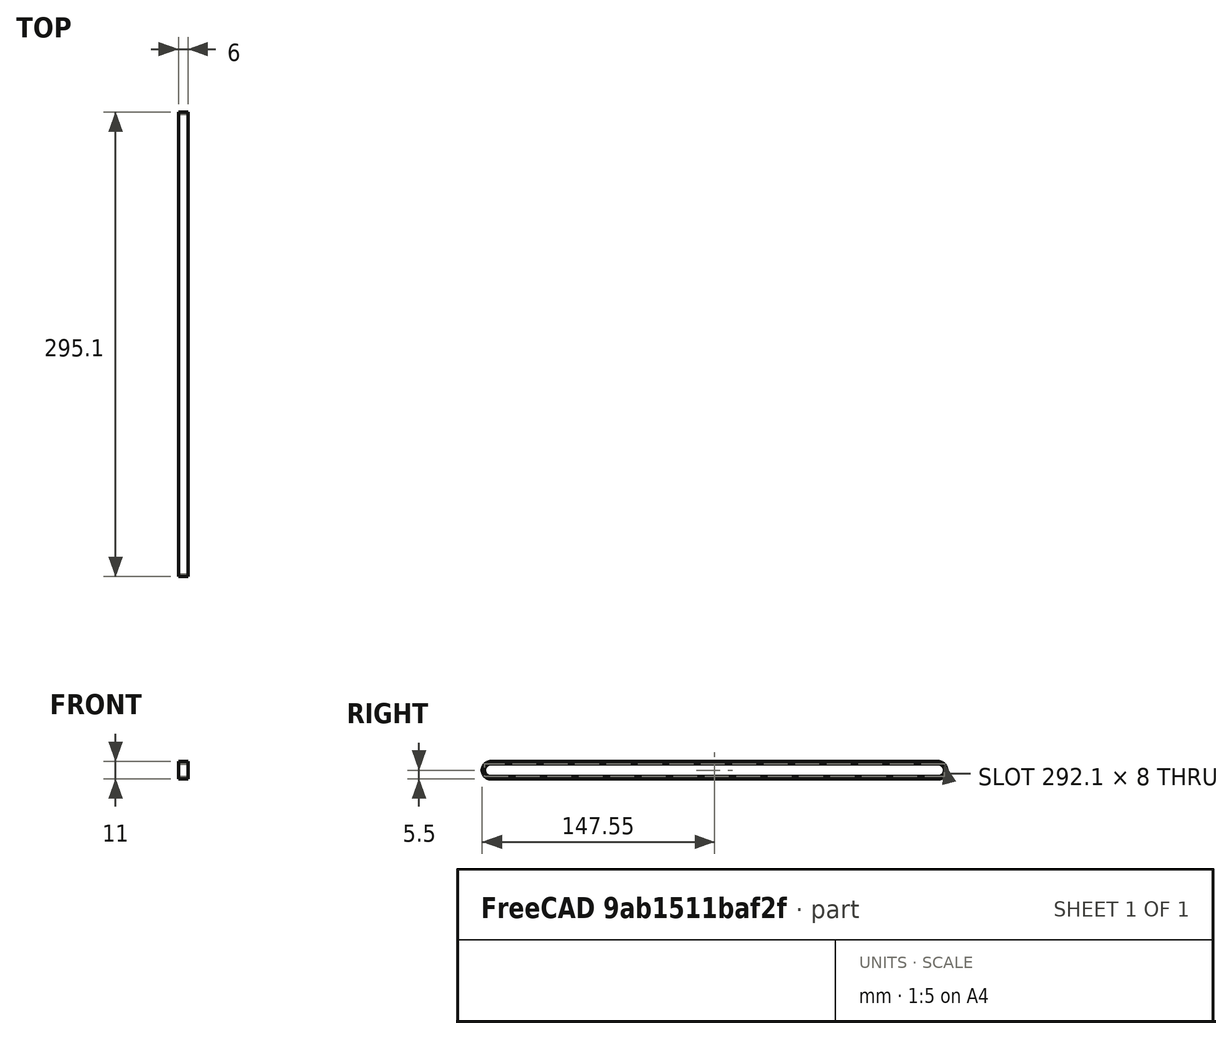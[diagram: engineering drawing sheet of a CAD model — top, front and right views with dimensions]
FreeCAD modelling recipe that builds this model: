
FCSTD DOCUMENT  (FreeCAD 0.18R16117 (Git))
Label: _GT2-Belt_Y-Axis
License: All rights reserved
LicenseURL: http://en.wikipedia.org/wiki/All_rights_reserved
objects: Sketcher::SketchObject×1, PartDesign::Pad×1, PartDesign::Body×1
note: 4 computed .brp shape members not serialized (recipe doc carries the construction recipe); baked Part::Feature solids carry a one-line shape summary decoded from their .brp

FEATURE [Sketcher::SketchObject] Sketch
  MapMode = 5
  Placement = pos=(0,0,0) rot=(0.57735,0.57735,0.57735;2.0944rad)
  Support = -> [YZ_Plane038]
  sketch-geometry (8):
    g0: LineSegment StartX=-140.25 StartY=5.5 StartZ=0 EndX=143.85 EndY=5.5 EndZ=0
    g1: LineSegment StartX=-140.25 StartY=4 StartZ=0 EndX=143.85 EndY=4 EndZ=0
    g2: LineSegment StartX=-140.25 StartY=-4 StartZ=0 EndX=143.85 EndY=-4 EndZ=0
    g3: LineSegment StartX=-140.25 StartY=-5.5 StartZ=0 EndX=143.85 EndY=-5.5 EndZ=0
    g4: ArcOfCircle CenterX=143.85 CenterY=0 CenterZ=0 NormalX=0 NormalY=0 NormalZ=1 AngleXU=0 Radius=4 StartAngle=4.71239 EndAngle=7.85398
    g5: ArcOfCircle CenterX=143.85 CenterY=0 CenterZ=0 NormalX=0 NormalY=0 NormalZ=1 AngleXU=0 Radius=5.5 StartAngle=4.71239 EndAngle=7.85398
    g6: ArcOfCircle CenterX=-140.25 CenterY=0 CenterZ=0 NormalX=0 NormalY=0 NormalZ=1 AngleXU=0 Radius=4 StartAngle=1.5708 EndAngle=4.71239
    g7: ArcOfCircle CenterX=-140.25 CenterY=0 CenterZ=0 NormalX=0 NormalY=0 NormalZ=1 AngleXU=0 Radius=5.5 StartAngle=1.5708 EndAngle=4.71239
  constraints (26):
    c: Horizontal(g0)
    c: Horizontal(g1)
    c: Horizontal(g2)
    c: Horizontal(g3)
    c: PointOnObject(g4,g-1)
    c: Coincident(g4,g1)
    c: Coincident(g4,g2)
    c: Coincident(g5,g4)
    c: Coincident(g5,g0)
    c: Coincident(g5,g3)
    c: Coincident(g6,g1)
    c: Coincident(g6,g2)
    c: Coincident(g7,g6)
    c: Coincident(g7,g0)
    c: Coincident(g7,g3)
    c: Tangent(g0,g7)
    c: Tangent(g7,g3)
    c: Tangent(g3,g5)
    c: Tangent(g4,g1)
    c: Tangent(g1,g6)
    c: DistanceX(g6,g4) = 284.1
    c: DistanceY(g3,g0) = 11
    c: DistanceY(g3,g2) = 1.5
    c: Tangent(g4,g2)
    c: Tangent(g0,g5)
    c: DistanceX(g-1,g4) = 143.85
FEATURE [PartDesign::Pad] Pad
  Length = 6
  Length2 = 100
  Midplane = true
  Placement = pos=(0,0,0) rot=(0.57735,0.57735,0.57735;2.0944rad)
  Profile = -> Sketch
  Type = 0
FEATURE [PartDesign::Body] Body  label="GT2-Belt_Y-Axis"
  Group = -> [Sketch,Pad]
  Origin = -> Origin038
  Placement = pos=(0,0,-1.4) rot=(0,0,1;0rad)
  Tip = -> Pad
